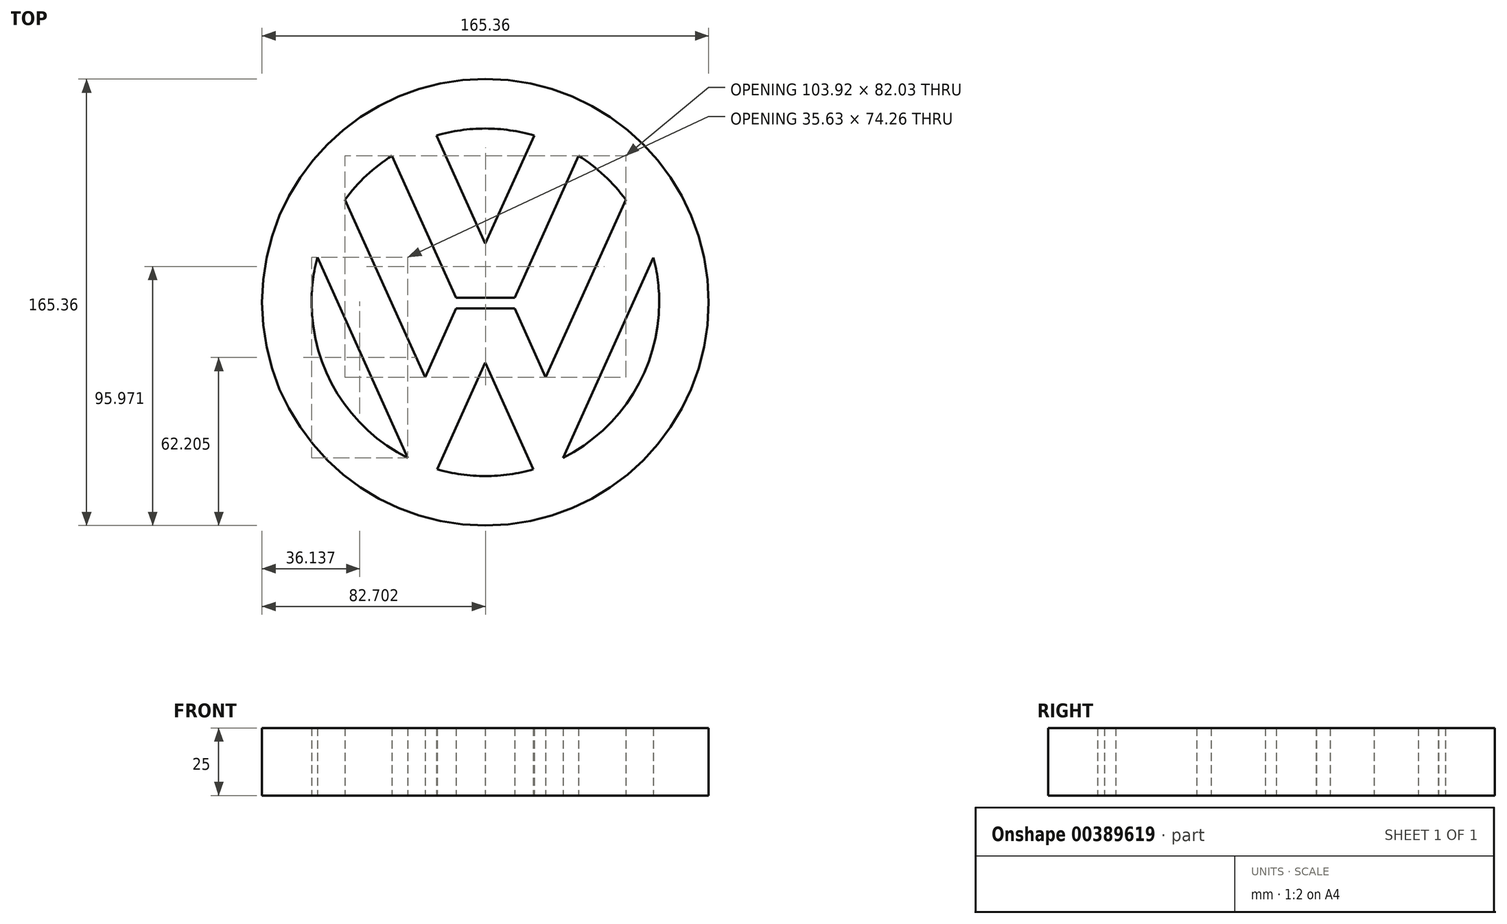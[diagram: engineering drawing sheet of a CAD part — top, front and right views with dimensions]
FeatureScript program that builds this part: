
annotation { "Feature Type Name" : "Feature", "Feature Type Description" : "" }
export const myFeature = defineFeature(function(context is Context, id is Id, definition is map)
    precondition{}
    {
        {
            var Q0;
            Q0=qCreatedBy(makeId("Top.planeOp"),FACE);
            var sketch = newSketch(context, id + "F0", { "sketchPlane" : qUnion([Q0])});
            skArc(sketch, "E0", {"start": v(82.68, 0) * mm, "mid": v(0, 82.68) * mm, "end": v(-82.68, 0) * mm});
            skArc(sketch, "E1", {"start": v(-82.68, 0) * mm, "mid": v(0, -82.68) * mm, "end": v(82.68, 0) * mm});
            skArc(sketch, "E2", {"start": v(28.73, -57.6) * mm, "mid": v(54.72, -33.86) * mm, "end": v(64.36, 0) * mm});
            skArc(sketch, "E3", {"start": v(64.36, 0) * mm, "mid": v(63.82, 8.33) * mm, "end": v(62.22, 16.52) * mm});
            skLineSegment(sketch, "E4", {"start": v(62.22, 16.52) * mm, "end": v(28.73, -57.6) * mm});
            skArc(sketch, "E5", {"start": v(-17.8, -61.86) * mm, "mid": v(-8.99, -63.74) * mm, "end": v(0, -64.36) * mm});
            skArc(sketch, "E6", {"start": v(0, -64.36) * mm, "mid": v(8.98, -63.73) * mm, "end": v(17.78, -61.87) * mm});
            skLineSegment(sketch, "E7", {"start": v(17.78, -61.87) * mm, "end": v(0, -22.38) * mm});
            skLineSegment(sketch, "E8", {"start": v(0, -22.38) * mm, "end": v(-17.8, -61.86) * mm});
            skArc(sketch, "E9", {"start": v(-62.18, 16.66) * mm, "mid": v(-63.82, 8.4) * mm, "end": v(-64.36, 0) * mm});
            skArc(sketch, "E10", {"start": v(-64.36, 0) * mm, "mid": v(-54.73, -33.87) * mm, "end": v(-28.73, -57.6) * mm});
            skLineSegment(sketch, "E11", {"start": v(-28.73, -57.6) * mm, "end": v(-62.18, 16.66) * mm});
            skLineSegment(sketch, "E12", {"start": v(34.55, 54.3) * mm, "end": v(10.92, 1.73) * mm});
            skLineSegment(sketch, "E13", {"start": v(10.92, 1.73) * mm, "end": v(-10.85, 1.73) * mm});
            skLineSegment(sketch, "E14", {"start": v(-10.85, 1.73) * mm, "end": v(-34.55, 54.3) * mm});
            skArc(sketch, "E15", {"start": v(-34.55, 54.3) * mm, "mid": v(-44, 46.97) * mm, "end": v(-51.94, 38.01) * mm});
            skLineSegment(sketch, "E16", {"start": v(-51.94, 38.01) * mm, "end": v(-22.3, -27.73) * mm});
            skLineSegment(sketch, "E17", {"start": v(-22.3, -27.73) * mm, "end": v(-10.85, -2.26) * mm});
            skLineSegment(sketch, "E18", {"start": v(-10.85, -2.26) * mm, "end": v(10.85, -2.26) * mm});
            skLineSegment(sketch, "E19", {"start": v(10.85, -2.26) * mm, "end": v(22.3, -27.73) * mm});
            skLineSegment(sketch, "E20", {"start": v(22.3, -27.73) * mm, "end": v(51.98, 37.95) * mm});
            skArc(sketch, "E21", {"start": v(51.98, 37.95) * mm, "mid": v(44.03, 46.94) * mm, "end": v(34.54, 54.3) * mm});
            skLineSegment(sketch, "E22", {"start": v(-18.1, 61.78) * mm, "end": v(0, 21.7) * mm});
            skLineSegment(sketch, "E23", {"start": v(0, 21.7) * mm, "end": v(18.08, 61.78) * mm});
            skArc(sketch, "E24", {"start": v(18.08, 61.78) * mm, "mid": v(9.13, 63.7) * mm, "end": v(0, 64.36) * mm});
            skArc(sketch, "E25", {"start": v(0, 64.36) * mm, "mid": v(-9.14, 63.71) * mm, "end": v(-18.1, 61.78) * mm});
            skSolve(sketch);
        }
        {
            var Q0;
            Q0 = qSketchRegion(id + "F0", true);
            extrude(context, id + "F1", {"entities" : qUnion([Q0]), "depth" : 25 * mm});
        }
    });
